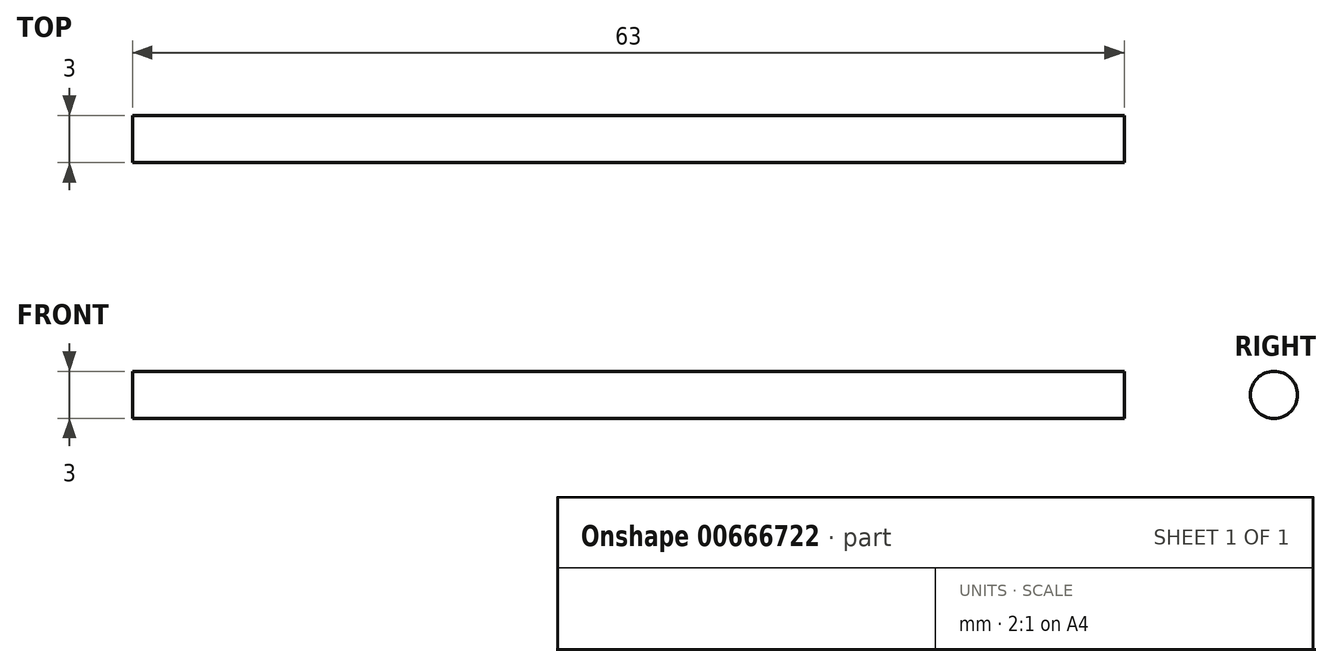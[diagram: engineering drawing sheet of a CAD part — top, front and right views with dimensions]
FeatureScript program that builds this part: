
annotation { "Feature Type Name" : "Feature", "Feature Type Description" : "" }
export const myFeature = defineFeature(function(context is Context, id is Id, definition is map)
    precondition{}
    {
        {
            var Q0;
            Q0=qCreatedBy(makeId("Right.planeOp"),FACE);
            var sketch = newSketch(context, id + "F0", { "sketchPlane" : qUnion([Q0])});
            skCircle(sketch, "E0", {"center": v(1, 1.12) * mm, "radius": 1.5 * mm});
            skPoint(sketch, "E0.first.point", {"position": v(0, 0) * mm});
            skSolve(sketch);
        }
        {
            var Q0;
            Q0=makeQuery(id+"F0.imprint","IMPRINT",FACE,{"disambiguationData":[TD([[makeQuery(id+"F0.imprint","IMPRINT",EDGE,{"derivedFrom":sQuery(id+"F0.wireOp",EDGE,"E0")}),1.0]])]});
            extrude(context, id + "F1", {"entities" : qUnion([Q0]), "depth" : 63 * mm, "offsetDistance" : 25 * mm});
        }
    });
